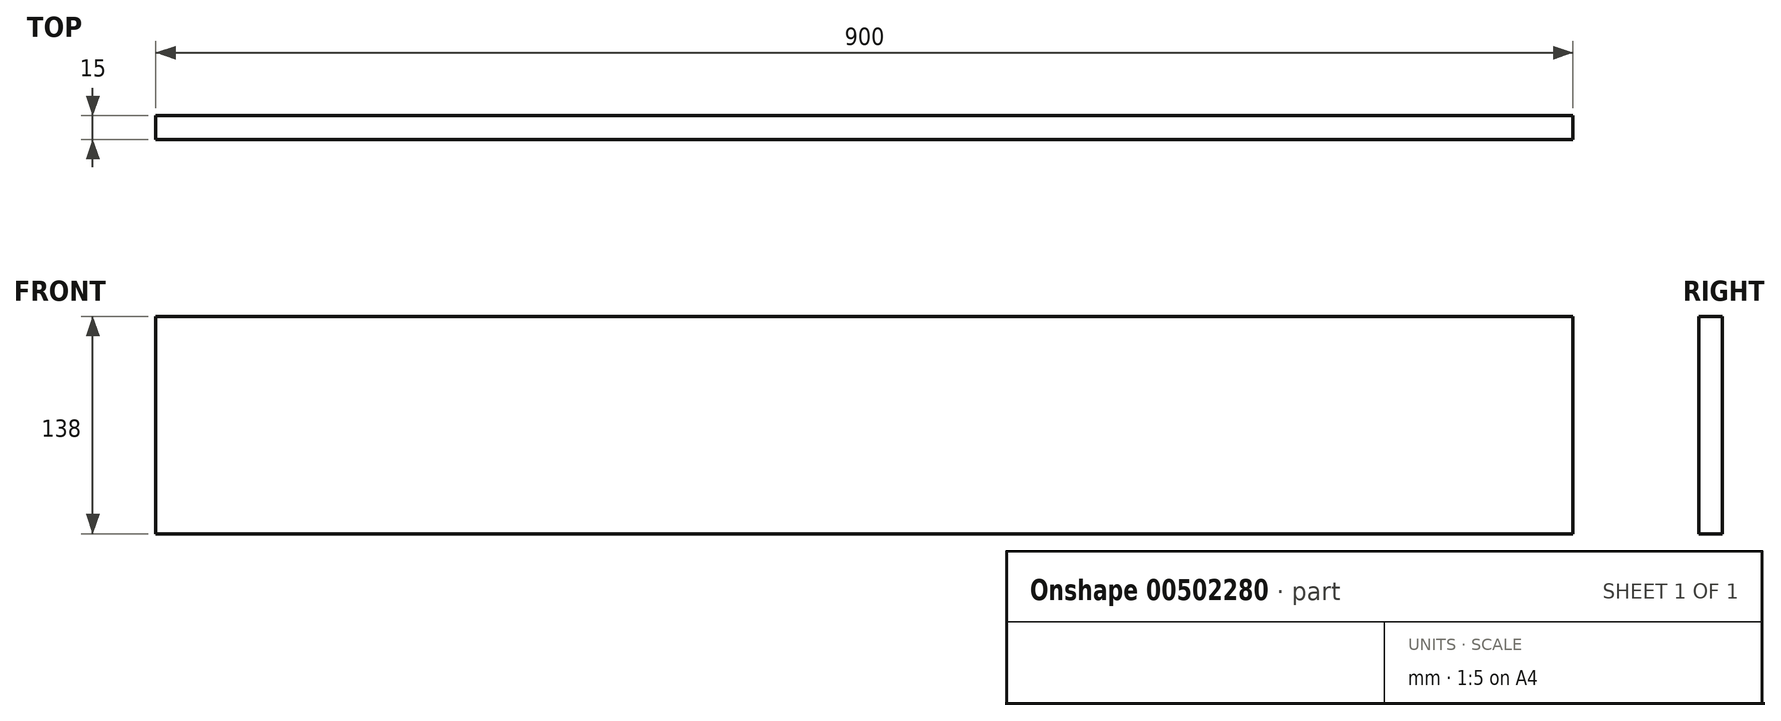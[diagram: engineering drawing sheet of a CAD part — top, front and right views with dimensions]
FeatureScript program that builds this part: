
annotation { "Feature Type Name" : "Feature", "Feature Type Description" : "" }
export const myFeature = defineFeature(function(context is Context, id is Id, definition is map)
    precondition{}
    {
        {
            var Q0;
            Q0=qCreatedBy(makeId("Front.planeOp"),FACE);
            var sketch = newSketch(context, id + "F0", { "sketchPlane" : qUnion([Q0])});
            skLineSegment(sketch, "E0.bottom", {"start": v(-1000.72, -164.49) * mm, "end": v(-100.72, -164.49) * mm});
            skLineSegment(sketch, "E0.top", {"start": v(-1000.72, -302.49) * mm, "end": v(-100.72, -302.49) * mm});
            skLineSegment(sketch, "E0.left", {"start": v(-1000.72, -164.49) * mm, "end": v(-1000.72, -302.49) * mm});
            skLineSegment(sketch, "E0.right", {"start": v(-100.72, -164.49) * mm, "end": v(-100.72, -302.49) * mm});
            skSolve(sketch);
        }
        {
            var Q0;
            Q0=makeQuery(id+"F0.imprint","IMPRINT",FACE,{"disambiguationData":[TD([[makeQuery(id+"F0.imprint","IMPRINT",EDGE,{"derivedFrom":sQuery(id+"F0.wireOp",EDGE,"E0.bottom")}),-1.0]])]});
            extrude(context, id + "F1", {"entities" : qUnion([Q0]), "depth" : 15 * mm});
        }
    });
